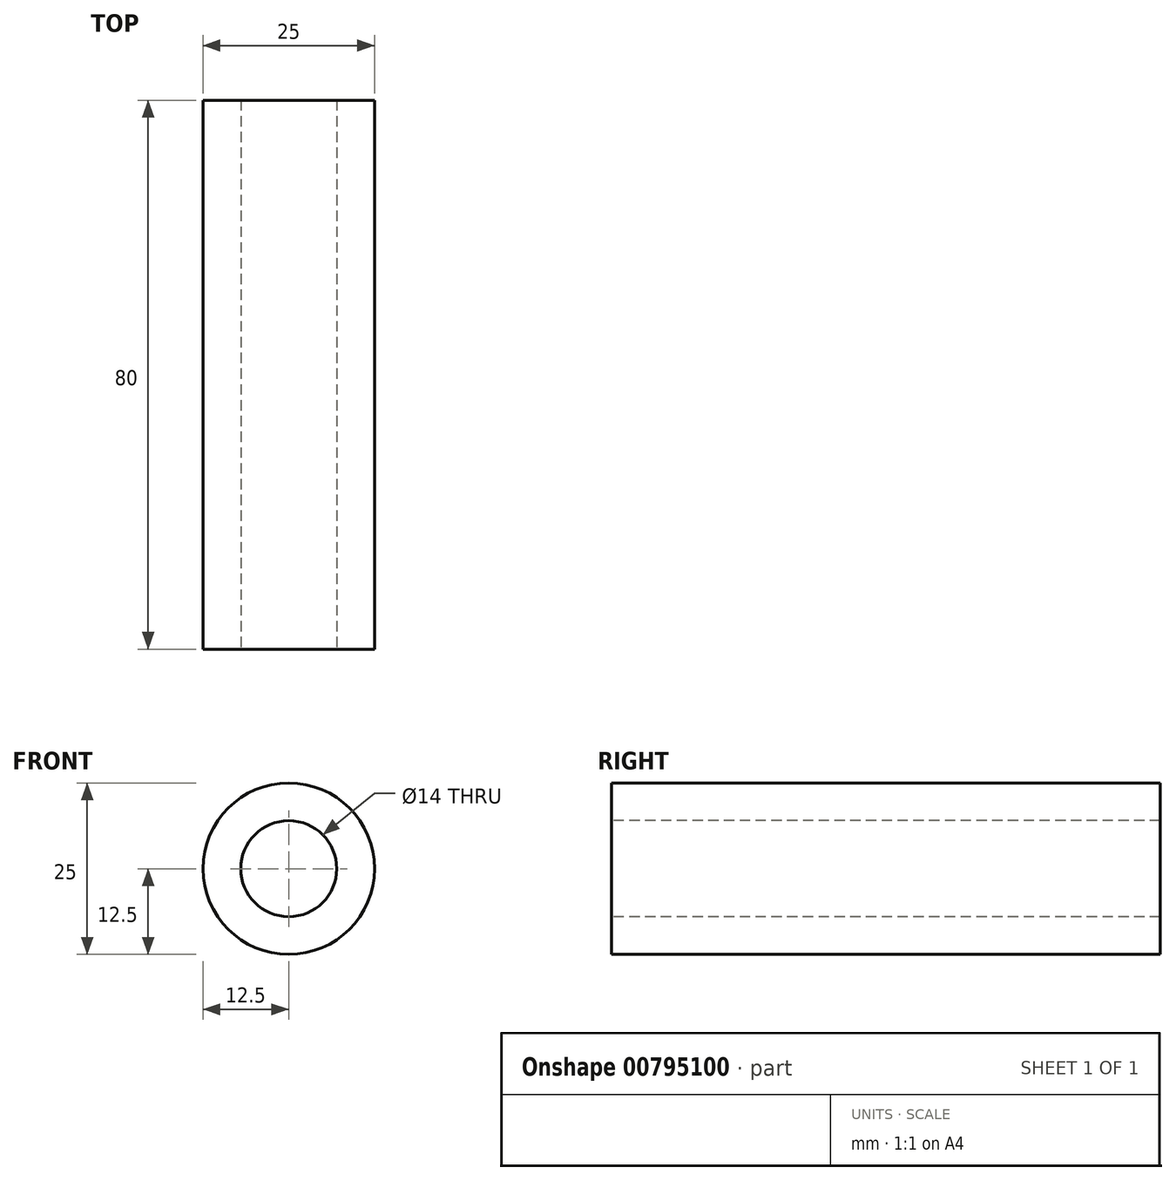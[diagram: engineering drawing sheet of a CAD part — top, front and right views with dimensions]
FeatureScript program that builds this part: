
annotation { "Feature Type Name" : "Feature", "Feature Type Description" : "" }
export const myFeature = defineFeature(function(context is Context, id is Id, definition is map)
    precondition{}
    {
        {
            var Q0;
            Q0=qCreatedBy(makeId("Front.planeOp"),FACE);
            var sketch = newSketch(context, id + "F0", { "sketchPlane" : qUnion([Q0])});
            skCircle(sketch, "E0", {"center": v(0, 0) * mm, "radius": 12.5 * mm});
            skSolve(sketch);
        }
        {
            var Q0;
            Q0=makeQuery(id+"F0.imprint","IMPRINT",FACE,{"disambiguationData":[TD([[makeQuery(id+"F0.imprint","IMPRINT",EDGE,{"derivedFrom":sQuery(id+"F0.wireOp",EDGE,"E0")}),1.0]])]});
            extrude(context, id + "F1", {"entities" : qUnion([Q0]), "oppositeDirection" : true, "depth" : 80 * mm, "offsetDistance" : 25.4 * mm});
        }
        {
            var Q0;
            Q0=makeQuery(id+"F1.opExtrude","CAP_FACE",FACE,{"disambiguationData":[OSD([sQuery(id+"F0.wireOp",EDGE,"E0")])],"isStart":true});
            var sketch = newSketch(context, id + "F2", { "sketchPlane" : qUnion([Q0])});
            skCircle(sketch, "E1", {"center": v(0, 0) * mm, "radius": 7 * mm});
            skSolve(sketch);
        }
        {
            var Q0;
            Q0 = qSketchRegion(id + "F2", true);
            extrude(context, id + "F3", {"entities" : qUnion([Q0]), "operationType" : NewBodyOperationType.REMOVE, "oppositeDirection" : true, "depth" : 101.6 * mm, "offsetDistance" : 25.4 * mm});
        }
    });
